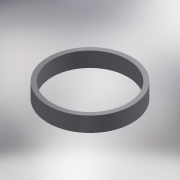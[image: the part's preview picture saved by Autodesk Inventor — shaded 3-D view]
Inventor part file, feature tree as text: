
AUTODESK INVENTOR PART (.ipt)
format: ipt  version: 2017 (Build 210142000, 142)  size: 125,952 bytes
history: native  units: mm
features: chamfer x2, extrude x1, sketch x1
ambient origin geometry x8: Origin, YZ Plane, XZ Plane, XY Plane, X Axis, Y Axis, Z Axis, Center Point
bodies: Solid1 (feature_tree)
feature tree (4):
  extrude  "Extrusion1"  Depth=7.0mm
  chamfer  "Chamfer1"  Distance=7.0mm
  chamfer  "Chamfer2"  Distance=0.6mm Angle=45.0deg
  sketch  "Sketch1"  dims[d0=39.0mm d1=35.0mm d2=7.0mm d3=0.0mm d4=0.6mm d5=2.0mm d6=45.0deg d7=0.2mm d8=2.0mm d9=45.0deg]
